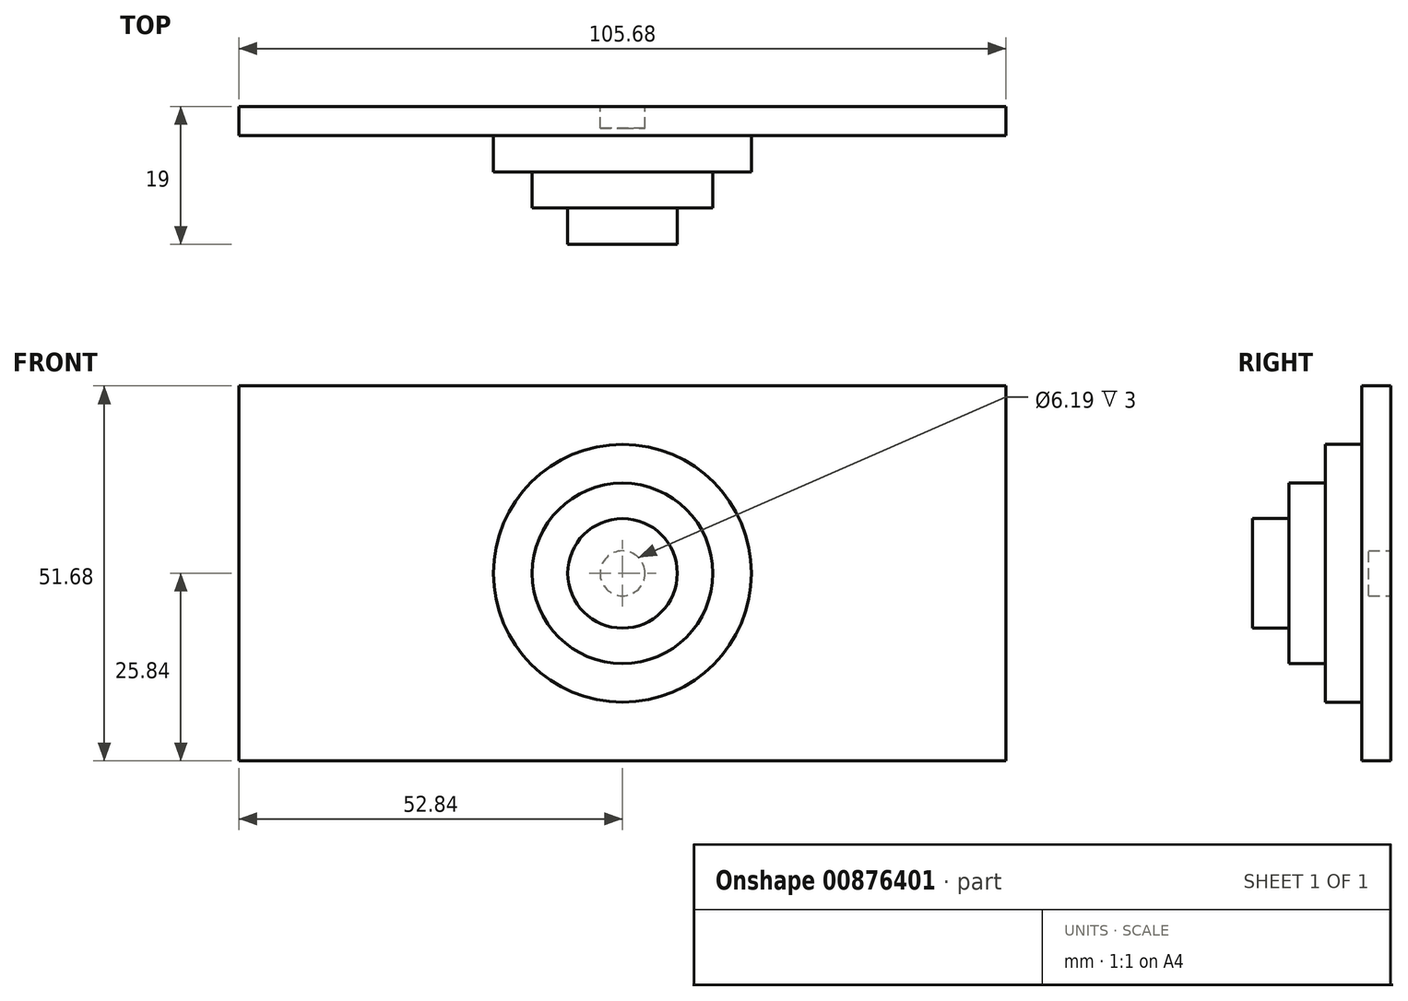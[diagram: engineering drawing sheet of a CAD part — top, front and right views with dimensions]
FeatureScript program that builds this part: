
annotation { "Feature Type Name" : "Feature", "Feature Type Description" : "" }
export const myFeature = defineFeature(function(context is Context, id is Id, definition is map)
    precondition{}
    {
        {
            var Q0;
            Q0=qCreatedBy(makeId("Front.planeOp"),FACE);
            var sketch = newSketch(context, id + "F0", { "sketchPlane" : qUnion([Q0])});
            skCircle(sketch, "E0", {"center": v(0, 0) * mm, "radius": 17.6 * mm});
            skCircle(sketch, "E1", {"center": v(0, 0) * mm, "radius": 12.52 * mm});
            skCircle(sketch, "E2", {"center": v(0, 0) * mm, "radius": 7.52 * mm});
            skCircle(sketch, "E3", {"center": v(0, 0) * mm, "radius": 3.2 * mm});
            skCircle(sketch, "E4", {"center": v(0, 0) * mm, "radius": 1.82 * mm});
            skLineSegment(sketch, "E5.bottom", {"start": v(-52.84, 25.84) * mm, "end": v(52.84, 25.84) * mm});
            skLineSegment(sketch, "E5.top", {"start": v(-52.84, -25.84) * mm, "end": v(52.84, -25.84) * mm});
            skLineSegment(sketch, "E5.left", {"start": v(-52.84, 25.84) * mm, "end": v(-52.84, -25.84) * mm});
            skLineSegment(sketch, "E5.right", {"start": v(52.84, 25.84) * mm, "end": v(52.84, -25.84) * mm});
            skSolve(sketch);
        }
        {
            var Q0;
            Q0=makeQuery(id+"F0.imprint","IMPRINT",FACE,{"disambiguationData":[TD([[makeQuery(id+"F0.imprint","IMPRINT",EDGE,{"derivedFrom":sQuery(id+"F0.wireOp",EDGE,"E0")}),-1.0]])]});
            var Q1;
            Q1=makeQuery(id+"F0.imprint","IMPRINT",FACE,{"disambiguationData":[TD([[makeQuery(id+"F0.imprint","IMPRINT",EDGE,{"derivedFrom":sQuery(id+"F0.wireOp",EDGE,"E2")}),1.0]])]});
            var Q2;
            Q2=makeQuery(id+"F0.imprint","IMPRINT",FACE,{"disambiguationData":[TD([[makeQuery(id+"F0.imprint","IMPRINT",EDGE,{"derivedFrom":sQuery(id+"F0.wireOp",EDGE,"E1")}),1.0]])]});
            var Q3;
            Q3=makeQuery(id+"F0.imprint","IMPRINT",FACE,{"disambiguationData":[TD([[makeQuery(id+"F0.imprint","IMPRINT",EDGE,{"derivedFrom":sQuery(id+"F0.wireOp",EDGE,"E0")}),1.0]])]});
            var Q4;
            Q4=makeQuery(id+"F0.imprint","IMPRINT",FACE,{"disambiguationData":[TD([[makeQuery(id+"F0.imprint","IMPRINT",EDGE,{"derivedFrom":sQuery(id+"F0.wireOp",EDGE,"E4")}),1.0]])]});
            var Q5;
            Q5=makeQuery(id+"F0.imprint","IMPRINT",FACE,{"disambiguationData":[TD([[makeQuery(id+"F0.imprint","IMPRINT",EDGE,{"derivedFrom":sQuery(id+"F0.wireOp",EDGE,"E3")}),1.0]])]});
            extrude(context, id + "F1", {"entities" : qUnion([Q0, Q1, Q2, Q3, Q4, Q5]), "depth" : 4 * mm, "offsetDistance" : 25 * mm});
        }
        {
            var Q0;
            Q0=makeQuery(id+"F1.opExtrude","CAP_FACE",FACE,{"disambiguationData":[OSD([sQuery(id+"F0.wireOp",EDGE,"E5.bottom"),sQuery(id+"F0.wireOp",EDGE,"E5.top"),sQuery(id+"F0.wireOp",EDGE,"E5.left"),sQuery(id+"F0.wireOp",EDGE,"E5.right")])],"isStart":false});
            var sketch = newSketch(context, id + "F2", { "sketchPlane" : qUnion([Q0])});
            skCircle(sketch, "E6", {"center": v(0, 0) * mm, "radius": 17.76 * mm});
            skSolve(sketch);
        }
        {
            var Q0;
            Q0 = qSketchRegion(id + "F2", true);
            extrude(context, id + "F3", {"entities" : qUnion([Q0]), "operationType" : NewBodyOperationType.ADD, "depth" : 5 * mm, "offsetDistance" : 25 * mm});
        }
        {
            var Q0;
            Q0=makeQuery(id+"F1.opExtrude","CAP_FACE",FACE,{"disambiguationData":[OSD([sQuery(id+"F0.wireOp",EDGE,"E5.bottom"),sQuery(id+"F0.wireOp",EDGE,"E5.top"),sQuery(id+"F0.wireOp",EDGE,"E5.left"),sQuery(id+"F0.wireOp",EDGE,"E5.right")])],"isStart":false});
            var sketch = newSketch(context, id + "F4", { "sketchPlane" : qUnion([Q0])});
            skCircle(sketch, "E7", {"center": v(0, 0) * mm, "radius": 12.44 * mm});
            skSolve(sketch);
        }
        {
            var Q0;
            Q0 = qSketchRegion(id + "F4", true);
            extrude(context, id + "F5", {"entities" : qUnion([Q0]), "operationType" : NewBodyOperationType.ADD, "depth" : 10 * mm, "offsetDistance" : 25 * mm});
        }
        {
            var Q0;
            Q0=makeQuery(id+"F1.opExtrude","CAP_FACE",FACE,{"disambiguationData":[OSD([sQuery(id+"F0.wireOp",EDGE,"E5.bottom"),sQuery(id+"F0.wireOp",EDGE,"E5.top"),sQuery(id+"F0.wireOp",EDGE,"E5.left"),sQuery(id+"F0.wireOp",EDGE,"E5.right")])],"isStart":false});
            var sketch = newSketch(context, id + "F6", { "sketchPlane" : qUnion([Q0])});
            skCircle(sketch, "E8", {"center": v(0, 0) * mm, "radius": 7.55 * mm});
            skSolve(sketch);
        }
        {
            var Q0;
            Q0 = qSketchRegion(id + "F6", true);
            extrude(context, id + "F7", {"entities" : qUnion([Q0]), "operationType" : NewBodyOperationType.ADD, "depth" : 15 * mm, "offsetDistance" : 25 * mm});
        }
        {
            var Q0;
            Q0=qCreatedBy(makeId("Front.planeOp"),FACE);
            var sketch = newSketch(context, id + "F8", { "sketchPlane" : qUnion([Q0])});
            skCircle(sketch, "E9", {"center": v(0, 0) * mm, "radius": 3.1 * mm});
            skSolve(sketch);
        }
        {
            var Q0;
            Q0 = qSketchRegion(id + "F8", true);
            extrude(context, id + "F9", {"entities" : qUnion([Q0]), "operationType" : NewBodyOperationType.REMOVE, "depth" : 3 * mm, "offsetDistance" : 25 * mm});
        }
    });
